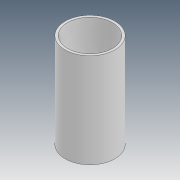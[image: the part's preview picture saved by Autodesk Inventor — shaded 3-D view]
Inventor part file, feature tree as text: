
AUTODESK INVENTOR PART (.ipt)
format: ipt  version: 2020 (Build 240168000, 168)  size: 101,376 bytes
history: native  units: mm
features: revolve x1, sketch x1
ambient origin geometry x8: Origin, YZ Plane, XZ Plane, XY Plane, X Axis, Y Axis, Z Axis, Center Point
bodies: Solid1 (feature_tree)
feature tree (2):
  revolve  "Revolution1"  [1 undecoded]
  sketch  "Sketch1"  dims[d0=21.0mm d1=10.66mm d2=11.185mm d3=1.2mm d4=0.0mm d5=5.0mm d6=90.0deg d7=90.0deg]
note: 1 required parameter value undecoded (feature->parameter linkage not recoverable at this tier; creation-order binding heuristic only, values carry confidence <= 0.55)
